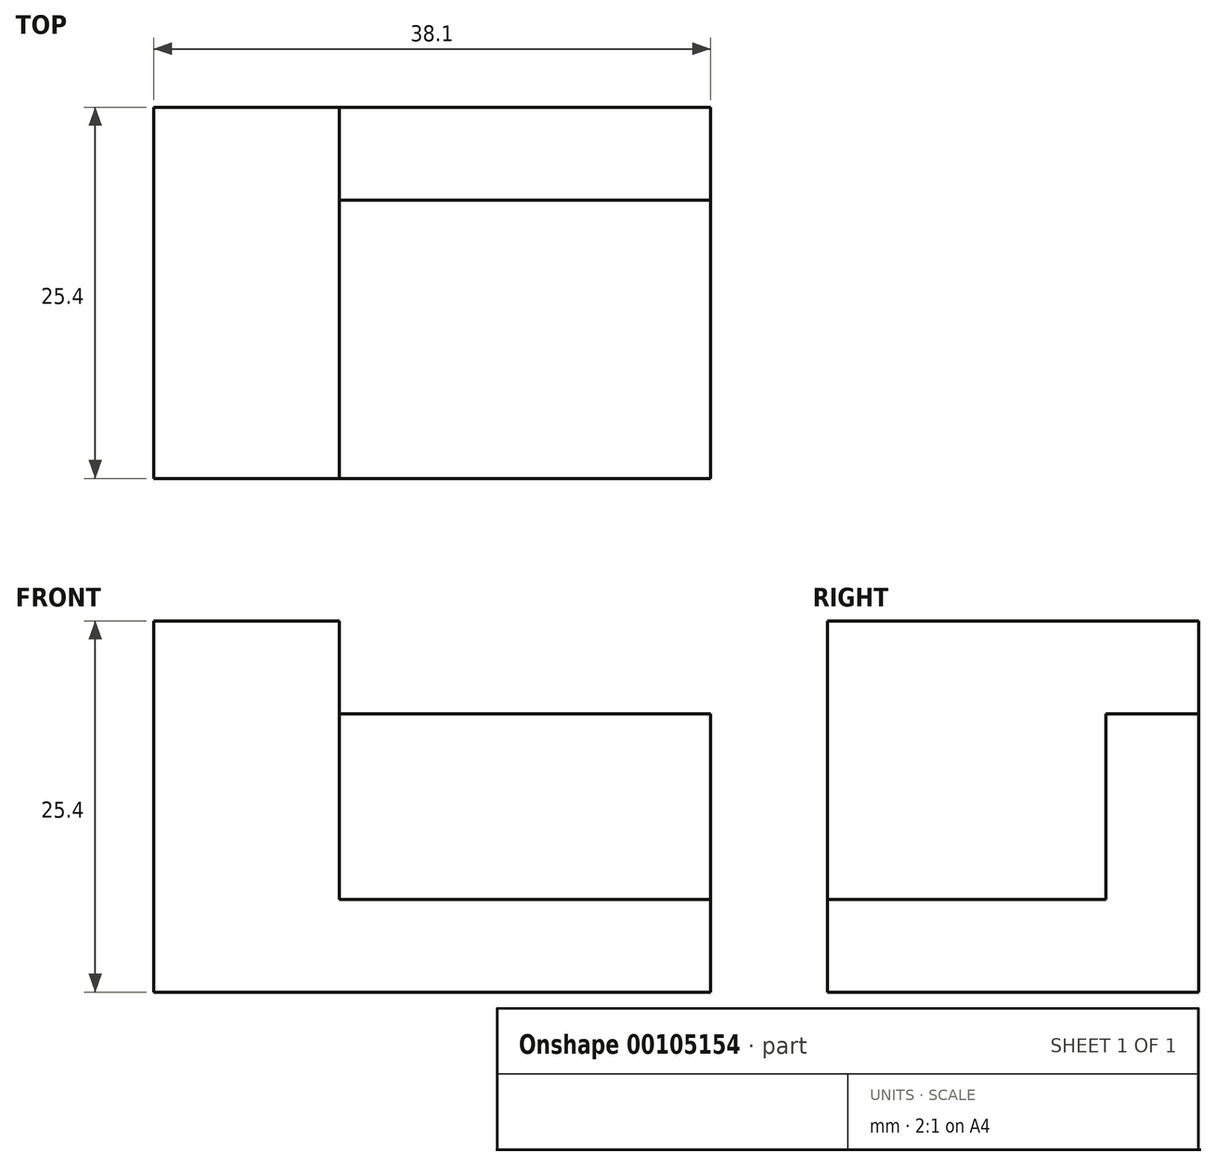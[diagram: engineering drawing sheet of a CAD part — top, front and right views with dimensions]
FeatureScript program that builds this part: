
annotation { "Feature Type Name" : "Feature", "Feature Type Description" : "" }
export const myFeature = defineFeature(function(context is Context, id is Id, definition is map)
    precondition{}
    {
        {
            var Q0;
            Q0=qCreatedBy(makeId("Front.planeOp"),FACE);
            var sketch = newSketch(context, id + "F0", { "sketchPlane" : qUnion([Q0])});
            skLineSegment(sketch, "E0.bottom", {"start": v(0, 0) * mm, "end": v(38.1, 0) * mm});
            skLineSegment(sketch, "E0.top", {"start": v(0, 25.4) * mm, "end": v(38.1, 25.4) * mm});
            skLineSegment(sketch, "E0.left", {"start": v(0, 0) * mm, "end": v(0, 25.4) * mm});
            skLineSegment(sketch, "E0.right", {"start": v(38.1, 0) * mm, "end": v(38.1, 25.4) * mm});
            skSolve(sketch);
        }
        {
            var Q0;
            Q0 = qSketchRegion(id + "F0", true);
            extrude(context, id + "F1", {"entities" : qUnion([Q0]), "endBound" : BoundingType.SYMMETRIC, "depth" : 25.4 * mm});
        }
        {
            var Q0;
            Q0=makeQuery(id+"F1.opExtrude","CAP_FACE",FACE,{"disambiguationData":[OSD([sQuery(id+"F0.wireOp",EDGE,"E0.bottom"),sQuery(id+"F0.wireOp",EDGE,"E0.top"),sQuery(id+"F0.wireOp",EDGE,"E0.left"),sQuery(id+"F0.wireOp",EDGE,"E0.right")])],"isStart":false});
            var sketch = newSketch(context, id + "F2", { "sketchPlane" : qUnion([Q0])});
            skLineSegment(sketch, "E1.bottom", {"start": v(12.7, 25.4) * mm, "end": v(38.1, 25.4) * mm});
            skLineSegment(sketch, "E1.top", {"start": v(12.7, 19.05) * mm, "end": v(38.1, 19.05) * mm});
            skLineSegment(sketch, "E1.left", {"start": v(12.7, 25.4) * mm, "end": v(12.7, 19.05) * mm});
            skLineSegment(sketch, "E1.right", {"start": v(38.1, 25.4) * mm, "end": v(38.1, 19.05) * mm});
            skSolve(sketch);
        }
        {
            var Q0;
            Q0=makeQuery(id+"F2.imprint","IMPRINT",FACE,{"disambiguationData":[TD([[makeQuery(id+"F2.imprint","IMPRINT",EDGE,{"derivedFrom":sQuery(id+"F2.wireOp",EDGE,"E1.bottom")}),-1.0]])]});
            extrude(context, id + "F3", {"entities" : qUnion([Q0]), "operationType" : NewBodyOperationType.REMOVE, "endBound" : BoundingType.THROUGH_ALL, "oppositeDirection" : true, "depth" : 25.4 * mm});
        }
        {
            var Q0;
            Q0=makeQuery(id+"F1.opExtrude","SWEPT_FACE",FACE,{"disambiguationData":[OSD([sQuery(id+"F0.wireOp",EDGE,"E0.right")])]});
            var sketch = newSketch(context, id + "F4", { "sketchPlane" : qUnion([Q0])});
            skLineSegment(sketch, "E2.bottom", {"start": v(-12.7, 19.05) * mm, "end": v(6.35, 19.05) * mm});
            skLineSegment(sketch, "E2.top", {"start": v(-12.7, 6.35) * mm, "end": v(6.35, 6.35) * mm});
            skLineSegment(sketch, "E2.left", {"start": v(-12.7, 19.05) * mm, "end": v(-12.7, 6.35) * mm});
            skLineSegment(sketch, "E2.right", {"start": v(6.35, 19.05) * mm, "end": v(6.35, 6.35) * mm});
            skSolve(sketch);
        }
        {
            var Q0;
            Q0=makeQuery(id+"F4.imprint","IMPRINT",FACE,{"disambiguationData":[TD([[makeQuery(id+"F4.imprint","IMPRINT",EDGE,{"derivedFrom":sQuery(id+"F4.wireOp",EDGE,"E2.bottom")}),1.0]])]});
            extrude(context, id + "F5", {"entities" : qUnion([Q0]), "operationType" : NewBodyOperationType.REMOVE, "oppositeDirection" : true, "depth" : 25.4 * mm});
        }
    });
